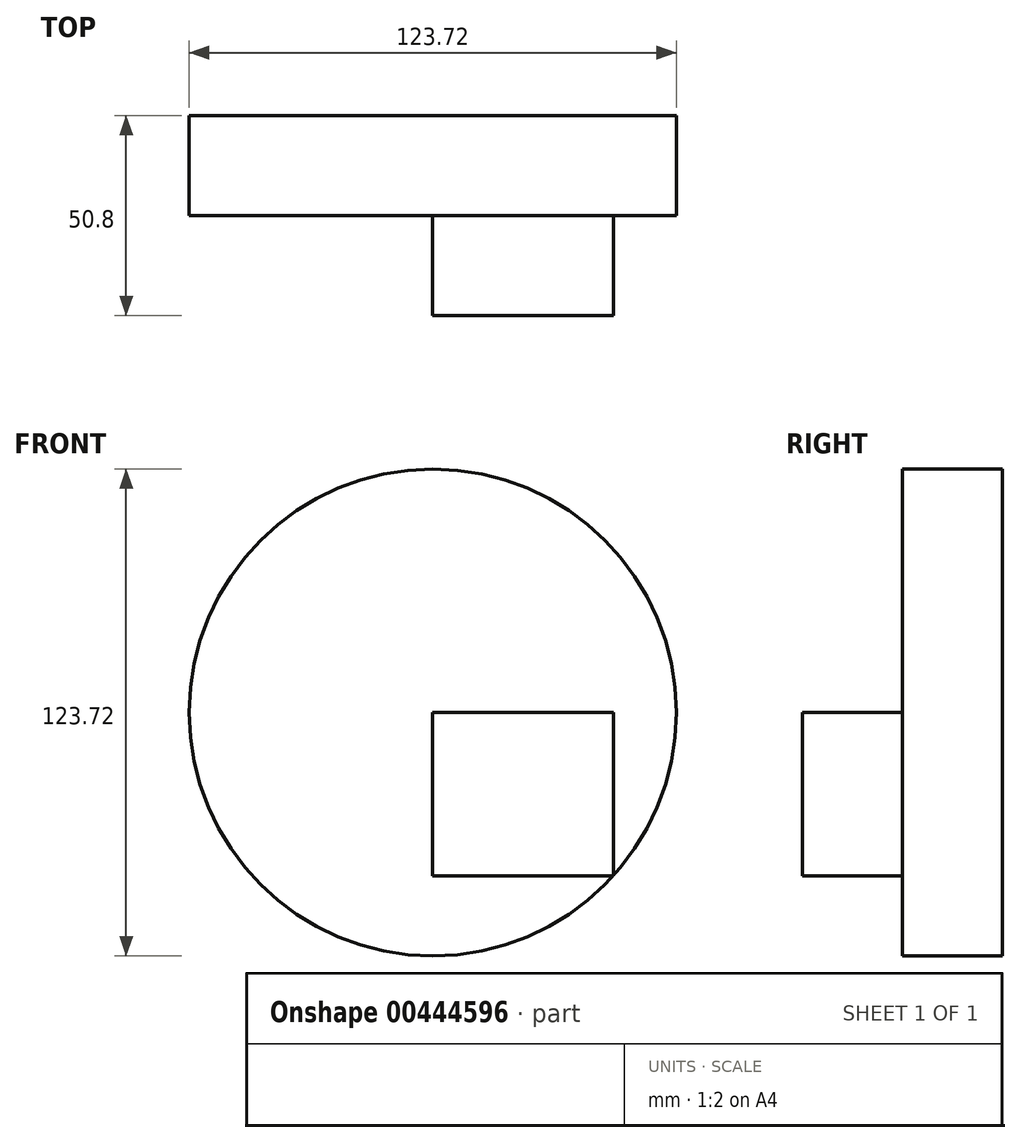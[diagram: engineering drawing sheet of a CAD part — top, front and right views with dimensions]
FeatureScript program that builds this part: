
annotation { "Feature Type Name" : "Feature", "Feature Type Description" : "" }
export const myFeature = defineFeature(function(context is Context, id is Id, definition is map)
    precondition{}
    {
        {
            var Q0;
            Q0=qCreatedBy(makeId("Front.planeOp"),FACE);
            var sketch = newSketch(context, id + "F0", { "sketchPlane" : qUnion([Q0])});
            skCircle(sketch, "E0", {"center": v(0, 0) * mm, "radius": 61.86 * mm});
            skSolve(sketch);
        }
        {
            var Q0;
            Q0=makeQuery(id+"F0.imprint","IMPRINT",FACE,{"disambiguationData":[TD([[makeQuery(id+"F0.imprint","IMPRINT",EDGE,{"derivedFrom":sQuery(id+"F0.wireOp",EDGE,"E0")}),1.0]])]});
            extrude(context, id + "F1", {"entities" : qUnion([Q0]), "depth" : 25.4 * mm});
        }
        {
            var Q0;
            Q0=makeQuery(id+"F1.opExtrude","CAP_FACE",FACE,{"disambiguationData":[OSD([sQuery(id+"F0.wireOp",EDGE,"E0")])],"isStart":false});
            var sketch = newSketch(context, id + "F2", { "sketchPlane" : qUnion([Q0])});
            skLineSegment(sketch, "E1.bottom", {"start": v(0, 0) * mm, "end": v(45.85, 0) * mm});
            skLineSegment(sketch, "E1.top", {"start": v(0, -41.52) * mm, "end": v(45.85, -41.52) * mm});
            skLineSegment(sketch, "E1.left", {"start": v(0, 0) * mm, "end": v(0, -41.52) * mm});
            skLineSegment(sketch, "E1.right", {"start": v(45.85, 0) * mm, "end": v(45.85, -41.52) * mm});
            skSolve(sketch);
        }
        {
            var Q0;
            Q0=makeQuery(id+"F2.imprint","IMPRINT",FACE,{"disambiguationData":[TD([[makeQuery(id+"F2.imprint","IMPRINT",EDGE,{"derivedFrom":sQuery(id+"F2.wireOp",EDGE,"E1.bottom")}),-1.0]])]});
            extrude(context, id + "F3", {"entities" : qUnion([Q0]), "operationType" : NewBodyOperationType.ADD, "depth" : 25.4 * mm});
        }
    });
